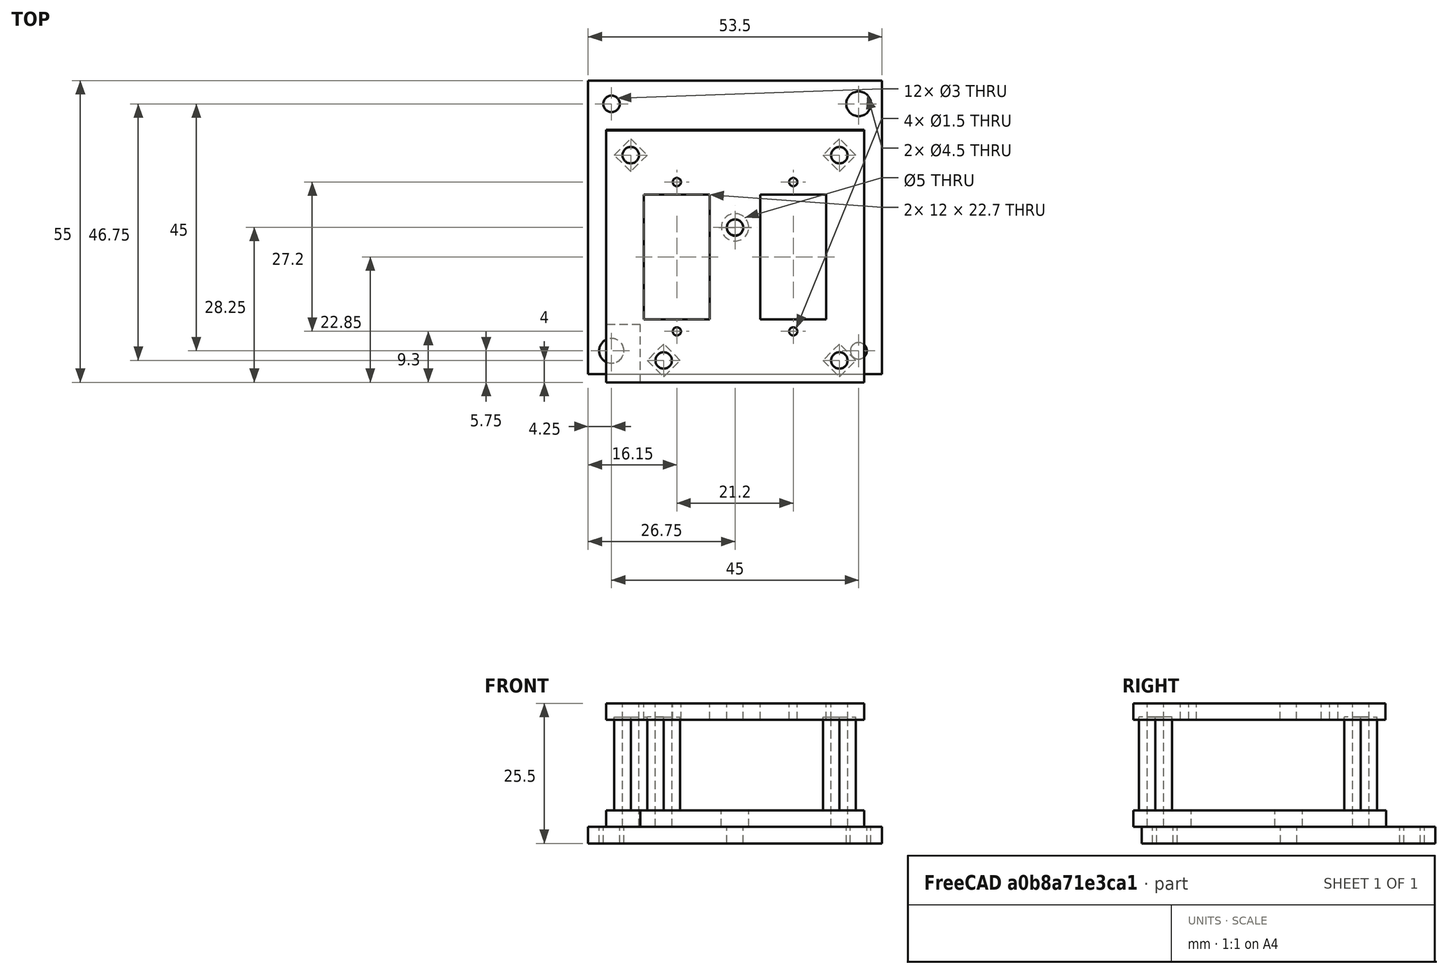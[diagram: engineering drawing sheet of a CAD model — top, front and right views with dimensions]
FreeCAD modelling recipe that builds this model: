
FCSTD DOCUMENT  (FreeCAD 0.17R13541 (Git))
Label: EGT APU Gauge
License: All rights reserved
LicenseURL: http://en.wikipedia.org/wiki/All_rights_reserved
objects: Part::Cylinder×12, Part::Cut×9, Part::FeaturePython×7, Part::Box×5, Part::Fuse×3, Part::Prism×3, Part::MultiFuse×3, Part::Mirroring×2
note: 44 computed .brp shape members not serialized (recipe doc carries the construction recipe); baked Part::Feature solids carry a one-line shape summary decoded from their .brp

FEATURE [Part::Box] Box  label="Placa original"
  AttacherType = Attacher::AttachEngine3D
  Height = 3
  Length = 53.5
  Width = 53.5
FEATURE [Part::Cylinder] Cylinder  label="Taladro 1"
  Angle = 360
  AttacherType = Attacher::AttachEngine3D
  Height = 10
  Placement = pos=(49.25,49.25,-4) rot=(0,0,1;0rad)
  Radius = 2.25
FEATURE [Part::FeaturePython] Array  label="Array taladro 1"  # Draft array (typed FeaturePython)
  Angle = 360
  ArrayType = 0
  Axis = (0,0,1)
  Base = -> Cylinder
  Center = (0,0,0)
  Fuse = false
  IntervalAxis = (0,0,0)
  IntervalX = (-45,-45,0)
  IntervalY = (0,1,0)
  IntervalZ = (0,0,0)
  NumberPolar = 1
  NumberX = 2
  NumberY = 1
  NumberZ = 1
FEATURE [Part::Cylinder] Cylinder001  label="Taladro 2"
  Angle = 360
  AttacherType = Attacher::AttachEngine3D
  Height = 10
  Placement = pos=(49.25,4.25,0) rot=(0,0,1;0rad)
  Radius = 1.5
FEATURE [Part::FeaturePython] Array001  label="Array taladro 2"  # Draft array (typed FeaturePython)
  Angle = 360
  ArrayType = 0
  Axis = (0,0,1)
  Base = -> Cylinder001
  Center = (0,0,0)
  Fuse = false
  IntervalAxis = (0,0,0)
  IntervalX = (-22.5,22.5,0)
  IntervalY = (0,1,0)
  IntervalZ = (0,0,0)
  NumberPolar = 1
  NumberX = 3
  NumberY = 1
  NumberZ = 1
FEATURE [Part::Fuse] Fusion  label="Taladros"
  Base = -> Array
  Refine = true
  Tool = -> Array001
FEATURE [Part::Cut] Cut  label="APU EGT Plate"
  Base = -> Box
  Refine = true
  Tool = -> Fusion
FEATURE [Part::Box] Box001  label="top plate 2"
  AttacherType = Attacher::AttachEngine3D
  Height = 3
  Length = 47
  Placement = pos=(3.25,-1.5,3) rot=(0,0,1;0rad)
  Width = 46
FEATURE [Part::Cylinder] Cylinder002  label="taladro 3"
  Angle = 360
  AttacherType = Attacher::AttachEngine3D
  Height = 10
  Placement = pos=(26.75,26.75,0) rot=(0,0,1;0rad)
  Radius = 2.5
FEATURE [Part::Cylinder] Cylinder003  label="taladro 4"
  Angle = 360
  AttacherType = Attacher::AttachEngine3D
  Height = 27
  Placement = pos=(7.75,2.5,0) rot=(0,0,1;0rad)
  Radius = 1.5
FEATURE [Part::FeaturePython] Array002  label="Array taladro 4"  # Draft array (typed FeaturePython)
  Angle = 360
  ArrayType = 0
  Axis = (0,0,1)
  Base = -> Cylinder003
  Center = (0,0,0)
  Fuse = false
  IntervalAxis = (0,0,0)
  IntervalX = (38,0,0)
  IntervalY = (0,37.4,0)
  IntervalZ = (0,0,0)
  NumberPolar = 1
  NumberX = 1
  NumberY = 2
  NumberZ = 1
FEATURE [Part::Prism] Prism  label="Columna"
  AttacherType = Attacher::AttachEngine3D
  Circumradius = 3
  Height = 20
  Placement = pos=(7.75,2.5,3) rot=(0,0,1;0rad)
  Polygon = 4
FEATURE [Part::FeaturePython] Array003  label="Array columnas"  # Draft array (typed FeaturePython)
  Angle = 360
  ArrayType = 0
  Axis = (0,0,1)
  Base = -> Prism
  Center = (0,0,0)
  Fuse = false
  IntervalAxis = (0,0,0)
  IntervalX = (38,0,0)
  IntervalY = (0,37.4,0)
  IntervalZ = (0,0,0)
  NumberPolar = 1
  NumberX = 1
  NumberY = 2
  NumberZ = 1
FEATURE [Part::Fuse] Fusion001  label="top plate columnas"
  Base = -> Box001
  Refine = true
  Tool = -> Array003
FEATURE [Part::Fuse] Fusion002  label="Taladros 2"
  Base = -> Cylinder002
  Refine = true
  Tool = -> Array002
FEATURE [Part::Cut] Cut001  label="Top plate"
  Base = -> Fusion001
  Refine = true
  Tool = -> Fusion002
FEATURE [Part::Box] Box002  label="base 2"
  AttacherType = Attacher::AttachEngine3D
  Height = 3
  Length = 47
  Placement = pos=(3.25,-1.5,22.5) rot=(0,0,1;0rad)
  Width = 45.9
FEATURE [Part::Box] Box003  label="Taladro servomotor"
  AttacherType = Attacher::AttachEngine3D
  Height = 10
  Length = 12
  Placement = pos=(10.15,10,19.5) rot=(0,0,1;0rad)
  Width = 22.7
FEATURE [Part::FeaturePython] Array004  label="Array taladro servomotor"  # Draft array (typed FeaturePython)
  Angle = 360
  ArrayType = 0
  Axis = (0,0,1)
  Base = -> Box003
  Center = (0,0,0)
  Fuse = false
  IntervalAxis = (0,0,0)
  IntervalX = (21.2,0,0)
  IntervalY = (0,1,0)
  IntervalZ = (0,0,0)
  NumberPolar = 1
  NumberX = 2
  NumberY = 1
  NumberZ = 1
FEATURE [Part::Cylinder] Cylinder004  label="taladro 5"
  Angle = 360
  AttacherType = Attacher::AttachEngine3D
  Height = 10
  Placement = pos=(7.75,2.5,19.5) rot=(0,0,1;0rad)
  Radius = 1.5
FEATURE [Part::FeaturePython] Array005  label="Array taladro 5"  # Draft array (typed FeaturePython)
  Angle = 360
  ArrayType = 0
  Axis = (0,0,1)
  Base = -> Cylinder004
  Center = (0,0,0)
  Fuse = false
  IntervalAxis = (0,0,0)
  IntervalX = (38,0,0)
  IntervalY = (0,37.4,0)
  IntervalZ = (0,0,0)
  NumberPolar = 1
  NumberX = 1
  NumberY = 2
  NumberZ = 1
FEATURE [Part::Cylinder] Cylinder005  label="Taladro 6"
  Angle = 360
  AttacherType = Attacher::AttachEngine3D
  Height = 10
  Placement = pos=(26.75,26.7,19.5) rot=(0,0,1;0rad)
  Radius = 1.5
FEATURE [Part::Cylinder] Cylinder006  label="Taladro 7"
  Angle = 360
  AttacherType = Attacher::AttachEngine3D
  Height = 10
  Placement = pos=(16.15,7.8,19.5) rot=(0,0,1;0rad)
  Radius = 0.75
FEATURE [Part::FeaturePython] Array006  label="Array taladros 7"  # Draft array (typed FeaturePython)
  Angle = 360
  ArrayType = 0
  Axis = (0,0,1)
  Base = -> Cylinder006
  Center = (0,0,0)
  Fuse = false
  IntervalAxis = (0,0,0)
  IntervalX = (21.2,0,0)
  IntervalY = (0,27.2,0)
  IntervalZ = (0,0,0)
  NumberPolar = 1
  NumberX = 2
  NumberY = 2
  NumberZ = 1
FEATURE [Part::MultiFuse] Fusion003  label="Taladros 3"
  Refine = true
  Shapes = -> [Cylinder005,Array006,Array004,Array005]
FEATURE [Part::Cut] Cut002  label="base previa"
  Base = -> Box002
  Refine = true
  Tool = -> Fusion003
FEATURE [Part::Prism] Prism001  label="Columna 3"
  AttacherType = Attacher::AttachEngine3D
  Circumradius = 3
  Height = 20
  Placement = pos=(45.75,39.9,3) rot=(0,0,1;0rad)
  Polygon = 4
FEATURE [Part::Cylinder] Cylinder007  label="taladro adicional 3"
  Angle = 360
  AttacherType = Attacher::AttachEngine3D
  Height = 27
  Placement = pos=(45.75,39.9,0) rot=(0,0,1;0rad)
  Radius = 1.5
FEATURE [Part::MultiFuse] Fusion004  label="placa con tres taladros"
  Refine = true
  Shapes = -> [Cut001,Prism001]
FEATURE [Part::Cut] Cut003  label="Placa con tres columnas"
  Base = -> Fusion004
  Refine = true
  Tool = -> Cylinder007
FEATURE [Part::Box] Box004  label="Recorte placa"
  AttacherType = Attacher::AttachEngine3D
  Height = 3
  Length = 10
  Placement = pos=(44,-2,3) rot=(0,0,1;0rad)
  Width = 11
FEATURE [Part::Cut] Cut004  label="Placa tres columnas y tornillo"
  Base = -> Cut003
  Refine = true
  Tool = -> Box004
FEATURE [Part::Prism] Prism002  label="Columna 4"
  AttacherType = Attacher::AttachEngine3D
  Circumradius = 3
  Height = 20
  Placement = pos=(39.75,2.5,3) rot=(0,0,1;0rad)
  Polygon = 4
FEATURE [Part::Cylinder] Cylinder008  label="taladro adicional 4"
  Angle = 360
  AttacherType = Attacher::AttachEngine3D
  Height = 27
  Placement = pos=(39.75,2.5,0) rot=(0,0,1;0rad)
  Radius = 1.5
FEATURE [Part::Cut] Cut005
  Base = -> Cut004
  Refine = true
  Tool = -> Cylinder008
FEATURE [Part::Cylinder] Cylinder009  label="taladro adicional 005"
  Angle = 360
  AttacherType = Attacher::AttachEngine3D
  Height = 27
  Placement = pos=(39.75,2.5,0) rot=(0,0,1;0rad)
  Radius = 1.5
FEATURE [Part::Cut] Cut006
  Base = -> Prism002
  Refine = true
  Tool = -> Cylinder009
FEATURE [Part::MultiFuse] Fusion005  label="top plate final"
  Refine = true
  Shapes = -> [Cut005,Cut006]
FEATURE [Part::Cylinder] Cylinder010  label="taladro 006"
  Angle = 360
  AttacherType = Attacher::AttachEngine3D
  Height = 10
  Placement = pos=(45.75,39.9,19.5) rot=(0,0,1;0rad)
  Radius = 1.5
FEATURE [Part::Cylinder] Cylinder011  label="taladro 007"
  Angle = 360
  AttacherType = Attacher::AttachEngine3D
  Height = 10
  Placement = pos=(39.75,2.5,18.5) rot=(0,0,1;0rad)
  Radius = 1.5
FEATURE [Part::Cut] Cut007  label="base 3 taladros"
  Base = -> Cut002
  Refine = true
  Tool = -> Cylinder010
FEATURE [Part::Cut] Cut008  label="base final"
  Base = -> Cut007
  Refine = true
  Tool = -> Cylinder011
FEATURE [Part::Mirroring] Part__Mirroring  label="top plate final (Mirror #1)"
  Base = (0,0,0)
  Normal = (1,0,0)
  Placement = pos=(53.5,0,0) rot=(0,0,1;0rad)
  Source = -> Fusion005
FEATURE [Part::Mirroring] Part__Mirroring001  label="base final (Mirror #2)"
  Base = (0,0,0)
  Normal = (1,0,0)
  Placement = pos=(53.5,0,0) rot=(0,0,1;0rad)
  Source = -> Cut008
